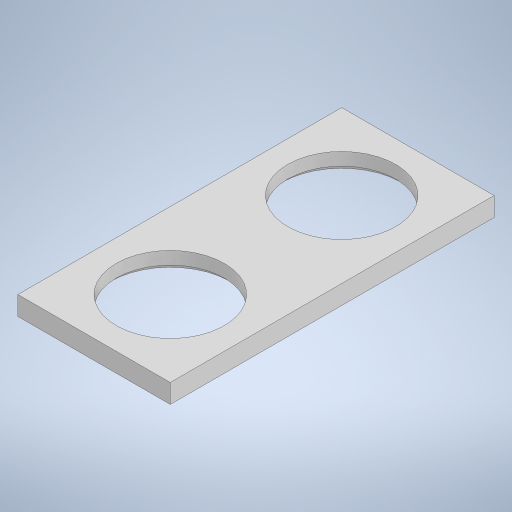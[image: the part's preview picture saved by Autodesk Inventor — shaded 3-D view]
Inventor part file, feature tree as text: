
AUTODESK INVENTOR PART (.ipt)
format: ipt  version: 2024.2 (Build 282272000, 272)  size: 238,080 bytes
history: native  units: mm
features: extrude x1, chamfer x1, sketch x1
ambient origin geometry x8: Origin, YZ Plane, XZ Plane, XY Plane, X Axis, Y Axis, Z Axis, Center Point
bodies: Solid1 (feature_tree)
feature tree (3):
  extrude  "Extrusion1"  Depth=3.0mm
  chamfer  "Chamfer1"  Distance=27.0mm
  sketch  "Sketch1"  dims[d0=17.0mm d1=17.0mm d2=27.0mm d3=12.0mm d4=12.0mm d5=12.0mm d6=12.0mm d7=3.0mm d8=0.0mm d9=1.0mm d10=2.0mm d11=45.0deg]
